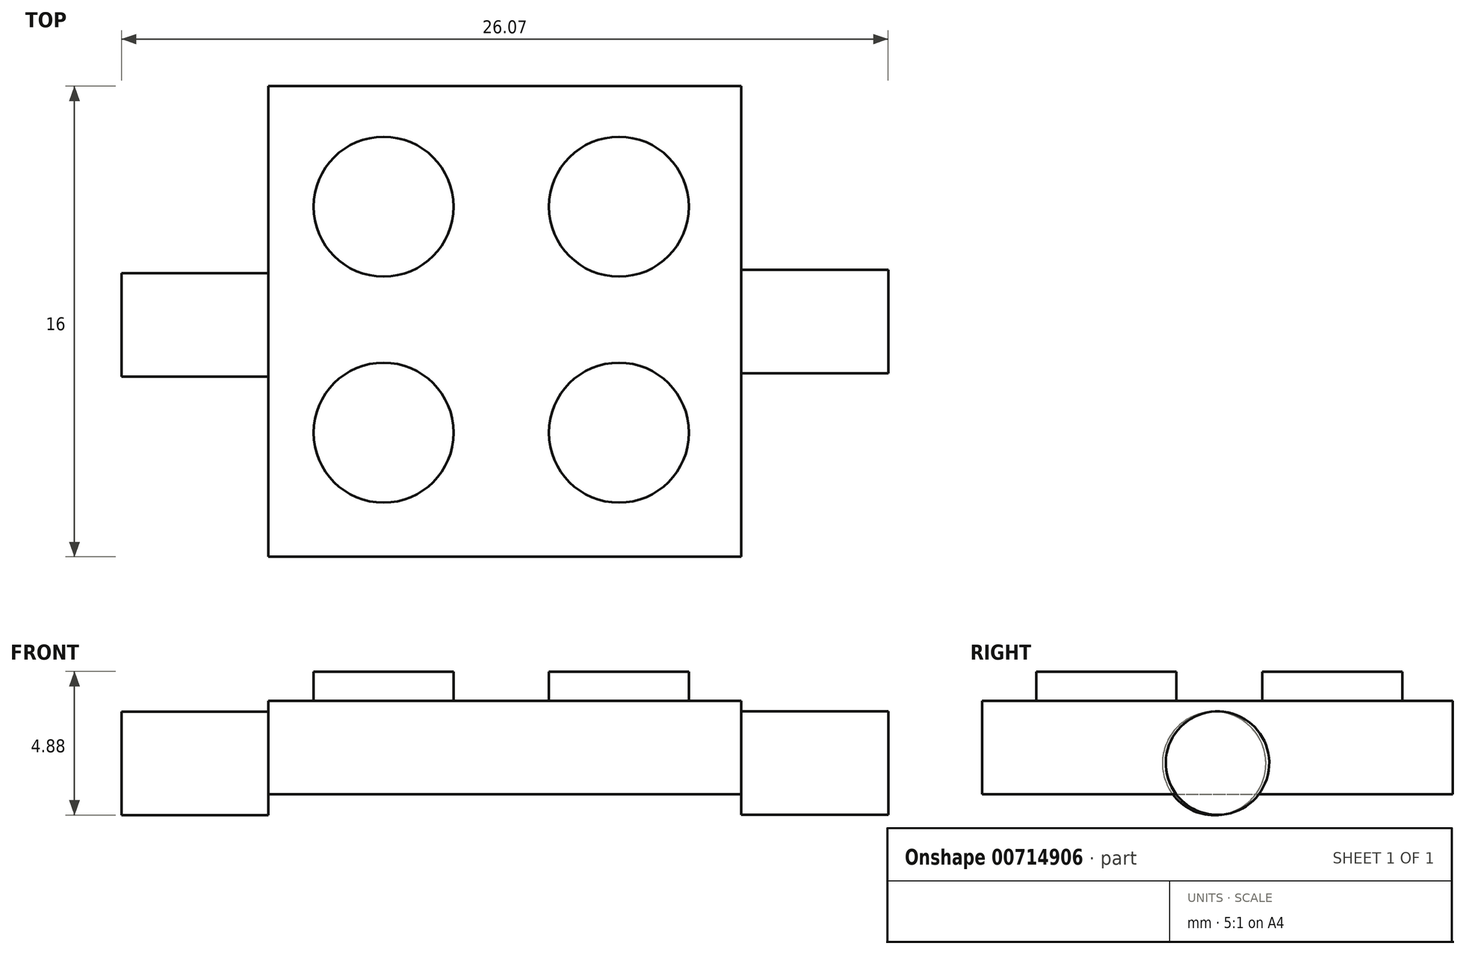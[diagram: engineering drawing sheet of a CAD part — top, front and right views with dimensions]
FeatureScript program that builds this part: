
annotation { "Feature Type Name" : "Feature", "Feature Type Description" : "" }
export const myFeature = defineFeature(function(context is Context, id is Id, definition is map)
    precondition{}
    {
        {
            var Q0;
            Q0=qCreatedBy(makeId("Front.planeOp"),FACE);
            var sketch = newSketch(context, id + "F0", { "sketchPlane" : qUnion([Q0])});
            skLineSegment(sketch, "E0", {"start": v(0, 0) * mm, "end": v(0, 3.17) * mm});
            skLineSegment(sketch, "E1", {"start": v(0, 3.17) * mm, "end": v(16.07, 3.17) * mm});
            skLineSegment(sketch, "E2", {"start": v(16.07, 3.17) * mm, "end": v(16.07, 0) * mm});
            skLineSegment(sketch, "E3", {"start": v(16.07, 0) * mm, "end": v(0, 0) * mm});
            skSolve(sketch);
        }
        {
            var Q0;
            Q0 = qSketchRegion(id + "F0", true);
            extrude(context, id + "F1", {"entities" : qUnion([Q0]), "depth" : 16 * mm, "offsetDistance" : 25 * mm});
        }
        {
            var Q0;
            Q0=makeQuery(id+"F1.opExtrude","SWEPT_FACE",FACE,{"disambiguationData":[OSD([sQuery(id+"F0.wireOp",EDGE,"E1")])]});
            var sketch = newSketch(context, id + "F2", { "sketchPlane" : qUnion([Q0])});
            skCircle(sketch, "E4", {"center": v(3.91, -11.78) * mm, "radius": 2.38 * mm});
            skCircle(sketch, "E5", {"center": v(11.92, -11.78) * mm, "radius": 2.38 * mm});
            skCircle(sketch, "E6", {"center": v(11.92, -4.1) * mm, "radius": 2.38 * mm});
            skCircle(sketch, "E7", {"center": v(3.91, -4.1) * mm, "radius": 2.38 * mm});
            skSolve(sketch);
        }
        {
            var Q0;
            Q0 = qSketchRegion(id + "F2", true);
            extrude(context, id + "F3", {"entities" : qUnion([Q0]), "operationType" : NewBodyOperationType.ADD, "depth" : 1 * mm, "offsetDistance" : 25 * mm});
        }
        {
            var Q0;
            Q0=makeQuery(id+"F1.opExtrude","SWEPT_FACE",FACE,{"disambiguationData":[OSD([sQuery(id+"F0.wireOp",EDGE,"E2")])]});
            var sketch = newSketch(context, id + "F4", { "sketchPlane" : qUnion([Q0])});
            skLineSegment(sketch, "E8", {"start": v(-16, 0) * mm, "end": v(-11.8, 0) * mm});
            skLineSegment(sketch, "E9", {"start": v(0, 0) * mm, "end": v(-4.25, 0) * mm});
            skLineSegment(sketch, "E10", {"start": v(-4.25, 0) * mm, "end": v(-4.25, 1.55) * mm});
            skLineSegment(sketch, "E11", {"start": v(-11.8, 0) * mm, "end": v(-11.8, 1.55) * mm});
            skLineSegment(sketch, "E12", {"start": v(-11.8, 1.55) * mm, "end": v(-9.74, 1.55) * mm});
            skLineSegment(sketch, "E13", {"start": v(-4.25, 1.55) * mm, "end": v(-6.3, 1.55) * mm});
            skCircle(sketch, "E14", {"center": v(-8, 1.05) * mm, "radius": 1.76 * mm});
            skLineSegment(sketch, "E15", {"start": v(-11.8, 0) * mm, "end": v(-9.4, 0) * mm});
            skLineSegment(sketch, "E16", {"start": v(-6.6, 0) * mm, "end": v(-4.25, 0) * mm});
            skSolve(sketch);
        }
        {
            var Q0;
            Q0 = qSketchRegion(id + "F4", true);
            extrude(context, id + "F5", {"entities" : qUnion([Q0]), "operationType" : NewBodyOperationType.ADD, "depth" : 5 * mm, "offsetDistance" : 25 * mm});
        }
        {
            var Q0;
            Q0=qCreatedBy(makeId("Right.planeOp"),FACE);
            var sketch = newSketch(context, id + "F6", { "sketchPlane" : qUnion([Q0])});
            skCircle(sketch, "E17", {"center": v(-8.12, 1.04) * mm, "radius": 1.76 * mm});
            skSolve(sketch);
        }
        {
            var Q0;
            Q0 = qSketchRegion(id + "F6", true);
            extrude(context, id + "F7", {"entities" : qUnion([Q0]), "operationType" : NewBodyOperationType.ADD, "oppositeDirection" : true, "depth" : 5 * mm, "offsetDistance" : 25 * mm});
        }
    });
